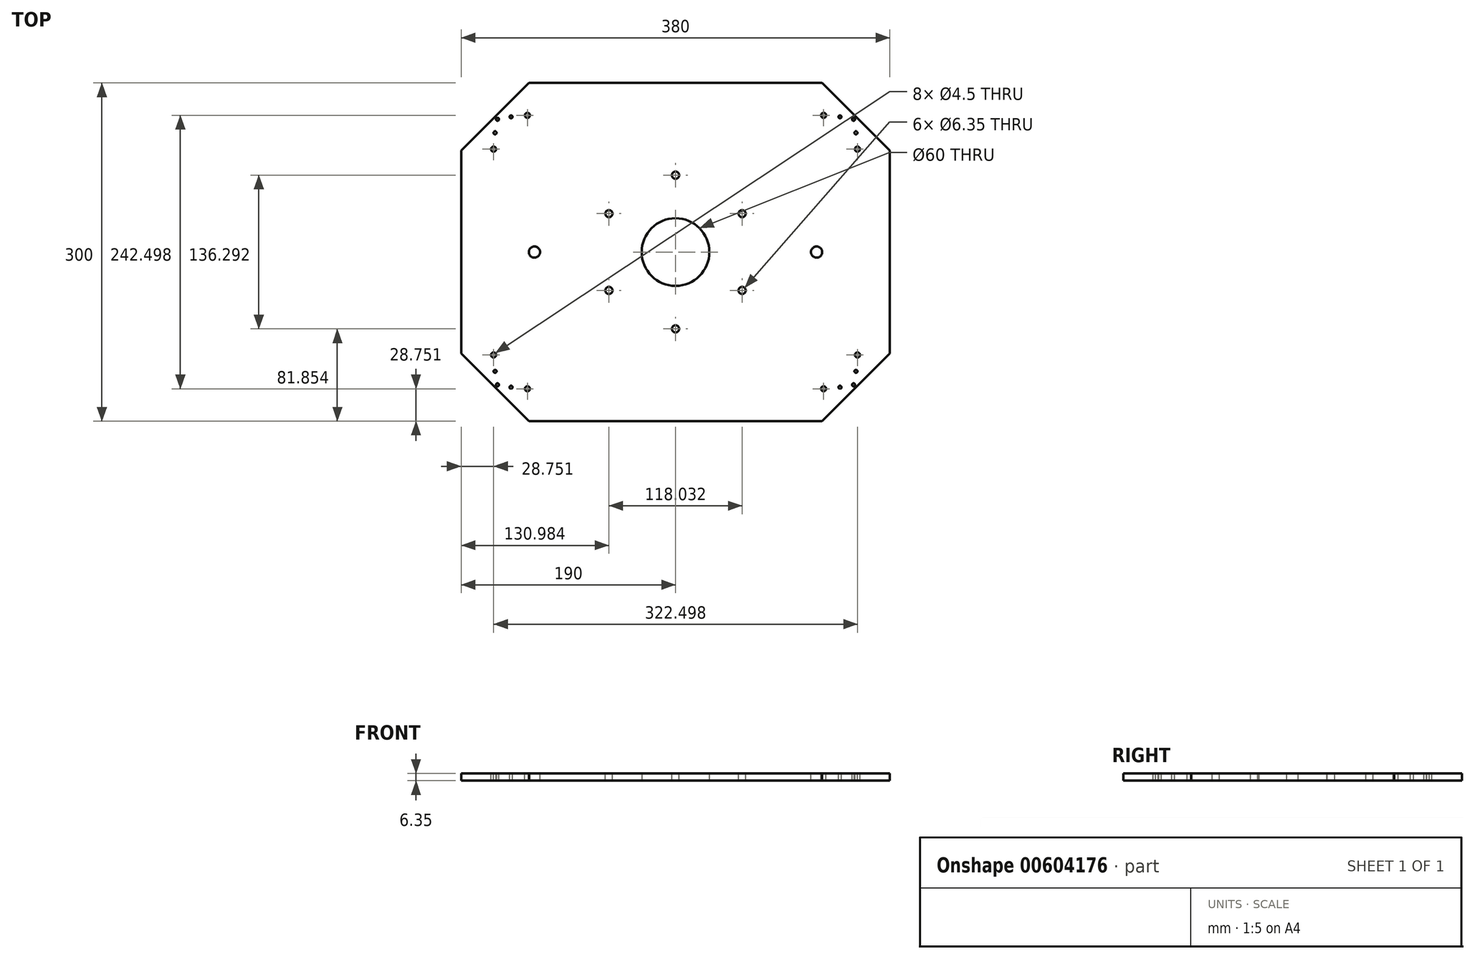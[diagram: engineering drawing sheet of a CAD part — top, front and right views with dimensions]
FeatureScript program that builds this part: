
annotation { "Feature Type Name" : "Feature", "Feature Type Description" : "" }
export const myFeature = defineFeature(function(context is Context, id is Id, definition is map)
    precondition{}
    {
        {
            var Q0;
            Q0=qCreatedBy(makeId("Top.planeOp"),FACE);
            var sketch = newSketch(context, id + "F0", { "sketchPlane" : qUnion([Q0])});
            skLineSegment(sketch, "E0", {"start": v(-130, 0) * mm, "end": v(-190, 60) * mm});
            skLineSegment(sketch, "E1", {"start": v(-190, 60) * mm, "end": v(-190, 240) * mm});
            skLineSegment(sketch, "E2", {"start": v(-190, 240) * mm, "end": v(-130, 300) * mm});
            skLineSegment(sketch, "E3", {"start": v(-130, 300) * mm, "end": v(130, 300) * mm});
            skLineSegment(sketch, "E4", {"start": v(130, 300) * mm, "end": v(190, 240) * mm});
            skLineSegment(sketch, "E5", {"start": v(190, 240) * mm, "end": v(190, 60) * mm});
            skLineSegment(sketch, "E6", {"start": v(190, 60) * mm, "end": v(130, 0) * mm});
            skLineSegment(sketch, "E7", {"start": v(130, 0) * mm, "end": v(-130, 0) * mm});
            skPoint(sketch, "E8.endSnap0", {"position": v(0, 300) * mm});
            skPoint(sketch, "E9.0.midPoint", {"position": v(0, 204.86) * mm});
            skPoint(sketch, "E10.0.midPoint", {"position": v(30.27, 157.38) * mm});
            skLineSegment(sketch, "E11", {"start": v(-190, 150) * mm, "end": v(190, 150) * mm, "construction": true});
            skLineSegment(sketch, "E12", {"start": v(0, 300) * mm, "end": v(0, 0) * mm, "construction": true});
            skCircle(sketch, "E13", {"center": v(0, 150) * mm, "radius": 30 * mm});
            skSolve(sketch);
        }
        {
            var Q0;
            Q0=qSketchRegion(id+"F0",true);
            extrude(context, id + "F1", {"entities" : qUnion([Q0]), "depth" : 6.35 * mm, "offsetDistance" : 25 * mm});
        }
        {
            var Q0;
            {var subQ0=sQuery(id+"F0.wireOp",EDGE,"E2");var subQ1=sQuery(id+"F0.wireOp",EDGE,"E1");var subQ2=sQuery(id+"F0.wireOp",EDGE,"E3");var subQ3=sQuery(id+"F0.wireOp",EDGE,"E0");var subQ4=sQuery(id+"F0.wireOp",EDGE,"E4");var subQ5=sQuery(id+"F0.wireOp",EDGE,"E5");var subQ6=sQuery(id+"F0.wireOp",EDGE,"E6");var subQ7=sQuery(id+"F0.wireOp",EDGE,"E7");Q0=makeQuery(id+"FAH0EIdtt6uSNSP_1.boolean.opBoolean","SPLIT",FACE,{"disambiguationData":[TD([makeQuery(id+"F1.opExtrude","SWEPT_FACE",FACE,{"disambiguationData":[OSD([subQ3])]})])],"derivedFrom":makeQuery(id+"F1.opExtrude","CAP_FACE",FACE,{"disambiguationData":[OSD([subQ3,subQ1,subQ0,subQ2,subQ4,subQ5,subQ6,subQ7,sQuery(id+"F0.wireOp",EDGE,"E10.0"),sQuery(id+"F0.wireOp",EDGE,"E10.1"),sQuery(id+"F0.wireOp",EDGE,"E10.2"),sQuery(id+"F0.wireOp",EDGE,"E10.3"),sQuery(id+"F0.wireOp",EDGE,"E10.4"),sQuery(id+"F0.wireOp",EDGE,"E10.5")])],"isStart":false})});}
            var sketch = newSketch(context, id + "F2", { "sketchPlane" : qUnion([Q0])});
            skLineSegment(sketch, "E14", {"start": v(-190, 150) * mm, "end": v(190, 150) * mm, "construction": true});
            skPoint(sketch, "E15", {"position": v(0, 150) * mm});
            skPoint(sketch, "E16", {"position": v(-125, 150) * mm});
            skPoint(sketch, "E17", {"position": v(125, 150) * mm});
            skSolve(sketch);
        }
        {
            var Q0;
            Q0=sQuery(id+"F2.wireOp",VERTEX,"E16");
            var Q1;
            Q1=sQuery(id+"F2.wireOp",VERTEX,"E17");
            var Q2;
            Q2=makeQuery(id+"F1.opExtrude","SWEPT_BODY",BODY,{"disambiguationData":[OSD([sQuery(id+"F0.wireOp",EDGE,"E0"),sQuery(id+"F0.wireOp",EDGE,"E1"),sQuery(id+"F0.wireOp",EDGE,"E2"),sQuery(id+"F0.wireOp",EDGE,"E3"),sQuery(id+"F0.wireOp",EDGE,"E4"),sQuery(id+"F0.wireOp",EDGE,"E5"),sQuery(id+"F0.wireOp",EDGE,"E6"),sQuery(id+"F0.wireOp",EDGE,"E7"),sQuery(id+"F0.wireOp",EDGE,"E10.0"),sQuery(id+"F0.wireOp",EDGE,"E10.1"),sQuery(id+"F0.wireOp",EDGE,"E10.2"),sQuery(id+"F0.wireOp",EDGE,"E10.3"),sQuery(id+"F0.wireOp",EDGE,"E10.4"),sQuery(id+"F0.wireOp",EDGE,"E10.5")])]});
            hole(context, id + "F3", {"style" : HoleStyle.SIMPLE, "endStyle" : HoleEndStyle.THROUGH, "holeDiameter" : 10 * mm, "majorDiameter" : 3.17 * mm, "isTappedThrough" : true, "tappedDepth" : 12 * mm, "tapClearance" : 3, "locations" : qUnion([Q0, Q1]), "scope" : qUnion([Q2])});
        }
        {
            var Q0;
            {var subQ0=sQuery(id+"F0.wireOp",EDGE,"E2");var subQ1=sQuery(id+"F0.wireOp",EDGE,"E1");var subQ2=sQuery(id+"F0.wireOp",EDGE,"E3");var subQ3=sQuery(id+"F0.wireOp",EDGE,"E0");var subQ4=sQuery(id+"F0.wireOp",EDGE,"E4");var subQ5=sQuery(id+"F0.wireOp",EDGE,"E5");var subQ6=sQuery(id+"F0.wireOp",EDGE,"E6");var subQ7=sQuery(id+"F0.wireOp",EDGE,"E7");Q0=makeQuery(id+"FAH0EIdtt6uSNSP_1.boolean.opBoolean","SPLIT",FACE,{"disambiguationData":[TD([makeQuery(id+"F1.opExtrude","SWEPT_FACE",FACE,{"disambiguationData":[OSD([subQ3])]})])],"derivedFrom":makeQuery(id+"F1.opExtrude","CAP_FACE",FACE,{"disambiguationData":[OSD([subQ3,subQ1,subQ0,subQ2,subQ4,subQ5,subQ6,subQ7,sQuery(id+"F0.wireOp",EDGE,"E10.0"),sQuery(id+"F0.wireOp",EDGE,"E10.1"),sQuery(id+"F0.wireOp",EDGE,"E10.2"),sQuery(id+"F0.wireOp",EDGE,"E10.3"),sQuery(id+"F0.wireOp",EDGE,"E10.4"),sQuery(id+"F0.wireOp",EDGE,"E10.5")])],"isStart":false})});}
            var sketch = newSketch(context, id + "F4", { "sketchPlane" : qUnion([Q0])});
            skLineSegment(sketch, "E18", {"start": v(0, 300) * mm, "end": v(0, 0) * mm, "construction": true});
            skLineSegment(sketch, "E19", {"start": v(-190, 150) * mm, "end": v(190, 150) * mm, "construction": true});
            skPoint(sketch, "E20", {"position": v(0, 150) * mm});
            skLineSegment(sketch, "E21", {"start": v(121.25, 261.25) * mm, "end": v(0, 261.25) * mm, "construction": true});
            skLineSegment(sketch, "E22", {"start": v(121.25, 261.25) * mm, "end": v(121.25, 150) * mm, "construction": true});
            skLineSegment(sketch, "E23", {"start": v(151.25, 231.25) * mm, "end": v(151.25, 150) * mm, "construction": true});
            skLineSegment(sketch, "E24", {"start": v(151.25, 231.25) * mm, "end": v(0, 231.25) * mm, "construction": true});
            skPoint(sketch, "E25", {"position": v(121.25, 231.25) * mm});
            skLineSegment(sketch, "E26", {"start": v(121.25, 231.25) * mm, "end": v(142.93, 252.93) * mm, "construction": true});
            skLineSegment(sketch, "E27", {"start": v(142.93, 252.93) * mm, "end": v(150, 245.86) * mm, "construction": true});
            skLineSegment(sketch, "E28", {"start": v(142.93, 252.93) * mm, "end": v(135.86, 260) * mm, "construction": true});
            skLineSegment(sketch, "E29", {"start": v(142.93, 252.93) * mm, "end": v(147.75, 257.75) * mm, "construction": true});
            skLineSegment(sketch, "E30.MirrorCS", {"start": v(-121.25, 261.25) * mm, "end": v(0, 261.25) * mm, "construction": true});
            skLineSegment(sketch, "E31.MirrorCS", {"start": v(-151.25, 231.25) * mm, "end": v(0, 231.25) * mm, "construction": true});
            skLineSegment(sketch, "E32.MirrorCS", {"start": v(-121.25, 261.25) * mm, "end": v(-121.25, 150) * mm, "construction": true});
            skLineSegment(sketch, "E33.MirrorCS", {"start": v(-151.25, 231.25) * mm, "end": v(-151.25, 150) * mm, "construction": true});
            skLineSegment(sketch, "E34.MirrorCS", {"start": v(-121.25, 231.25) * mm, "end": v(-142.93, 252.93) * mm, "construction": true});
            skLineSegment(sketch, "E35.MirrorCS", {"start": v(-142.93, 252.93) * mm, "end": v(-135.86, 260) * mm, "construction": true});
            skLineSegment(sketch, "E36.MirrorCS", {"start": v(-142.93, 252.93) * mm, "end": v(-150, 245.86) * mm, "construction": true});
            skLineSegment(sketch, "E37.MirrorCS", {"start": v(-142.93, 252.93) * mm, "end": v(-147.75, 257.75) * mm, "construction": true});
            skLineSegment(sketch, "E38.MirrorCS", {"start": v(-142.93, 47.07) * mm, "end": v(-147.75, 42.25) * mm, "construction": true});
            skLineSegment(sketch, "E39.MirrorCS", {"start": v(-142.93, 47.07) * mm, "end": v(-135.86, 40) * mm, "construction": true});
            skLineSegment(sketch, "E40.MirrorCS", {"start": v(-142.93, 47.07) * mm, "end": v(-150, 54.14) * mm, "construction": true});
            skLineSegment(sketch, "E41.MirrorCS", {"start": v(-121.25, 68.75) * mm, "end": v(-142.93, 47.07) * mm, "construction": true});
            skLineSegment(sketch, "E42.MirrorCS", {"start": v(-151.25, 68.75) * mm, "end": v(0, 68.75) * mm, "construction": true});
            skLineSegment(sketch, "E43.MirrorCS", {"start": v(-151.25, 68.75) * mm, "end": v(-151.25, 150) * mm, "construction": true});
            skLineSegment(sketch, "E44.MirrorCS", {"start": v(-121.25, 38.75) * mm, "end": v(0, 38.75) * mm, "construction": true});
            skLineSegment(sketch, "E45.MirrorCS", {"start": v(-121.25, 38.75) * mm, "end": v(-121.25, 150) * mm, "construction": true});
            skLineSegment(sketch, "E46.MirrorCS", {"start": v(151.25, 68.75) * mm, "end": v(0, 68.75) * mm, "construction": true});
            skLineSegment(sketch, "E47.MirrorCS", {"start": v(121.25, 38.75) * mm, "end": v(0, 38.75) * mm, "construction": true});
            skLineSegment(sketch, "E48.MirrorCS", {"start": v(121.25, 38.75) * mm, "end": v(121.25, 150) * mm, "construction": true});
            skLineSegment(sketch, "E49.MirrorCS", {"start": v(151.25, 68.75) * mm, "end": v(151.25, 150) * mm, "construction": true});
            skLineSegment(sketch, "E50.MirrorCS", {"start": v(121.25, 68.75) * mm, "end": v(142.93, 47.07) * mm, "construction": true});
            skLineSegment(sketch, "E51.MirrorCS", {"start": v(142.93, 47.07) * mm, "end": v(150, 54.14) * mm, "construction": true});
            skLineSegment(sketch, "E52.MirrorCS", {"start": v(142.93, 47.07) * mm, "end": v(135.86, 40) * mm, "construction": true});
            skLineSegment(sketch, "E53.MirrorCS", {"start": v(142.93, 47.07) * mm, "end": v(147.75, 42.25) * mm, "construction": true});
            skLineSegment(sketch, "E54", {"start": v(-160, 270) * mm, "end": v(-157.75, 267.75) * mm, "construction": true});
            skLineSegment(sketch, "E55", {"start": v(-160, 30) * mm, "end": v(-157.75, 32.25) * mm, "construction": true});
            skLineSegment(sketch, "E56", {"start": v(160, 270) * mm, "end": v(157.75, 267.75) * mm, "construction": true});
            skLineSegment(sketch, "E57", {"start": v(160, 30) * mm, "end": v(157.75, 32.25) * mm, "construction": true});
            skLineSegment(sketch, "E58", {"start": v(160, 30) * mm, "end": v(130, 0) * mm, "construction": true});
            skLineSegment(sketch, "E59", {"start": v(130, 0) * mm, "end": v(145, 15) * mm, "construction": true});
            skLineSegment(sketch, "E60", {"start": v(145, 15) * mm, "end": v(131.25, 28.75) * mm, "construction": true});
            skLineSegment(sketch, "E61", {"start": v(190, 60) * mm, "end": v(160, 30) * mm, "construction": true});
            skLineSegment(sketch, "E62", {"start": v(175, 45) * mm, "end": v(161.25, 58.75) * mm, "construction": true});
            skLineSegment(sketch, "E63.MirrorCS", {"start": v(-145, 15) * mm, "end": v(-131.25, 28.75) * mm, "construction": true});
            skLineSegment(sketch, "E64.MirrorCS", {"start": v(-175, 45) * mm, "end": v(-161.25, 58.75) * mm, "construction": true});
            skLineSegment(sketch, "E65.MirrorCS", {"start": v(-145, 285) * mm, "end": v(-131.25, 271.25) * mm, "construction": true});
            skLineSegment(sketch, "E66.MirrorCS", {"start": v(-175, 255) * mm, "end": v(-161.25, 241.25) * mm, "construction": true});
            skLineSegment(sketch, "E67.MirrorCS", {"start": v(145, 285) * mm, "end": v(131.25, 271.25) * mm, "construction": true});
            skLineSegment(sketch, "E68.MirrorCS", {"start": v(175, 255) * mm, "end": v(161.25, 241.25) * mm, "construction": true});
            skLineSegment(sketch, "E69", {"start": v(-150, 245.86) * mm, "end": v(-148.23, 244.1) * mm, "construction": true});
            skLineSegment(sketch, "E70", {"start": v(-135.86, 260) * mm, "end": v(-134.1, 258.23) * mm, "construction": true});
            skLineSegment(sketch, "E71.MirrorCS", {"start": v(-150, 54.14) * mm, "end": v(-148.23, 55.9) * mm, "construction": true});
            skLineSegment(sketch, "E72.MirrorCS", {"start": v(-135.86, 40) * mm, "end": v(-134.1, 41.77) * mm, "construction": true});
            skLineSegment(sketch, "E73.MirrorCS", {"start": v(150, 245.86) * mm, "end": v(148.23, 244.1) * mm, "construction": true});
            skLineSegment(sketch, "E74.MirrorCS", {"start": v(135.86, 260) * mm, "end": v(134.1, 258.23) * mm, "construction": true});
            skLineSegment(sketch, "E75.MirrorCS", {"start": v(150, 54.14) * mm, "end": v(148.23, 55.9) * mm, "construction": true});
            skLineSegment(sketch, "E76.MirrorCS", {"start": v(135.86, 40) * mm, "end": v(134.1, 41.77) * mm, "construction": true});
            skLineSegment(sketch, "E77", {"start": v(-135.86, 40) * mm, "end": v(-145.76, 30.1) * mm, "construction": true});
            skLineSegment(sketch, "E78", {"start": v(-150, 54.14) * mm, "end": v(-159.9, 44.24) * mm, "construction": true});
            skLineSegment(sketch, "E79.MirrorCS", {"start": v(150, 54.14) * mm, "end": v(159.9, 44.24) * mm, "construction": true});
            skLineSegment(sketch, "E80.MirrorCS", {"start": v(135.86, 40) * mm, "end": v(145.76, 30.1) * mm, "construction": true});
            skLineSegment(sketch, "E81.MirrorCS", {"start": v(-150, 245.86) * mm, "end": v(-159.9, 255.76) * mm, "construction": true});
            skLineSegment(sketch, "E82.MirrorCS", {"start": v(-135.86, 260) * mm, "end": v(-145.76, 269.9) * mm, "construction": true});
            skLineSegment(sketch, "E83.MirrorCS", {"start": v(150, 245.86) * mm, "end": v(159.9, 255.76) * mm, "construction": true});
            skLineSegment(sketch, "E84.MirrorCS", {"start": v(135.86, 260) * mm, "end": v(145.76, 269.9) * mm, "construction": true});
            skSolve(sketch);
        }
        {
            var Q0;
            Q0=makeQuery(id+"F4.imprint","IMPRINT",FACE,{"disambiguationData":[TD([[makeQuery(id+"F4.imprint","IMPRINT",EDGE,{"derivedFrom":makeQuery(id+"F1.opExtrude","CAP_EDGE",EDGE,{"disambiguationData":[OSD([sQuery(id+"F0.wireOp",EDGE,"E0")])],"isStart":false})}),-1.0]])]});
            var sketch = newSketch(context, id + "F5", { "sketchPlane" : qUnion([Q0])});
            skCircle(sketch, "E85.cCircle", {"center": v(0, 150) * mm, "radius": 59.02 * mm, "construction": true});
            skLineSegment(sketch, "E85.0", {"start": v(0, 218.15) * mm, "end": v(59.02, 184.07) * mm});
            skLineSegment(sketch, "E85.1", {"start": v(59.02, 184.07) * mm, "end": v(59.02, 115.93) * mm});
            skLineSegment(sketch, "E85.2", {"start": v(59.02, 115.93) * mm, "end": v(0, 81.85) * mm});
            skLineSegment(sketch, "E85.3", {"start": v(0, 81.85) * mm, "end": v(-59.02, 115.93) * mm});
            skLineSegment(sketch, "E85.4", {"start": v(-59.02, 115.93) * mm, "end": v(-59.02, 184.07) * mm});
            skLineSegment(sketch, "E85.5", {"start": v(-59.02, 184.07) * mm, "end": v(0, 218.15) * mm});
            skPoint(sketch, "E85.0.midPoint", {"position": v(29.5, 201.1) * mm});
            skSolve(sketch);
        }
        {
            var Q0;
            Q0=sQuery(id+"F5.wireOp",VERTEX,"E85.5.end");
            var Q1;
            Q1=sQuery(id+"F5.wireOp",VERTEX,"E85.0.end");
            var Q2;
            Q2=sQuery(id+"F5.wireOp",VERTEX,"E85.5.start");
            var Q3;
            Q3=sQuery(id+"F5.wireOp",VERTEX,"E85.4.start");
            var Q4;
            Q4=sQuery(id+"F5.wireOp",VERTEX,"E85.2.end");
            var Q5;
            Q5=sQuery(id+"F5.wireOp",VERTEX,"E85.1.end");
            var Q6;
            Q6=makeQuery(id+"F1.opExtrude","SWEPT_BODY",BODY,{"disambiguationData":[OSD([sQuery(id+"F0.wireOp",EDGE,"E0"),sQuery(id+"F0.wireOp",EDGE,"E1"),sQuery(id+"F0.wireOp",EDGE,"E2"),sQuery(id+"F0.wireOp",EDGE,"E3"),sQuery(id+"F0.wireOp",EDGE,"E4"),sQuery(id+"F0.wireOp",EDGE,"E5"),sQuery(id+"F0.wireOp",EDGE,"E6"),sQuery(id+"F0.wireOp",EDGE,"E7"),sQuery(id+"F0.wireOp",EDGE,"E13")])]});
            hole(context, id + "F6", {"style" : HoleStyle.SIMPLE, "endStyle" : HoleEndStyle.THROUGH, "holeDiameter" : 6.35 * mm, "majorDiameter" : 3 * mm, "isTappedThrough" : true, "tappedDepth" : 12 * mm, "tapClearance" : 3, "locations" : qUnion([Q0, Q1, Q2, Q3, Q4, Q5]), "scope" : qUnion([Q6])});
        }
        {
            var Q0;
            Q0=sQuery(id+"F4.wireOp",VERTEX,"E66.MirrorCS.end");
            var Q1;
            Q1=sQuery(id+"F4.wireOp",VERTEX,"E65.MirrorCS.end");
            var Q2;
            Q2=sQuery(id+"F4.wireOp",VERTEX,"E64.MirrorCS.end");
            var Q3;
            Q3=sQuery(id+"F4.wireOp",VERTEX,"E63.MirrorCS.end");
            var Q4;
            Q4=sQuery(id+"F4.wireOp",VERTEX,"E60.end");
            var Q5;
            Q5=sQuery(id+"F4.wireOp",VERTEX,"E62.end");
            var Q6;
            Q6=sQuery(id+"F4.wireOp",VERTEX,"E68.MirrorCS.end");
            var Q7;
            Q7=sQuery(id+"F4.wireOp",VERTEX,"E67.MirrorCS.end");
            var Q8;
            Q8=makeQuery(id+"F1.opExtrude","SWEPT_BODY",BODY,{"disambiguationData":[OSD([sQuery(id+"F0.wireOp",EDGE,"E0"),sQuery(id+"F0.wireOp",EDGE,"E1"),sQuery(id+"F0.wireOp",EDGE,"E2"),sQuery(id+"F0.wireOp",EDGE,"E3"),sQuery(id+"F0.wireOp",EDGE,"E4"),sQuery(id+"F0.wireOp",EDGE,"E5"),sQuery(id+"F0.wireOp",EDGE,"E6"),sQuery(id+"F0.wireOp",EDGE,"E7"),sQuery(id+"F0.wireOp",EDGE,"E13")])]});
            hole(context, id + "F7", {"style" : HoleStyle.SIMPLE, "endStyle" : HoleEndStyle.THROUGH, "holeDiameter" : 4.5 * mm, "majorDiameter" : 5 * mm, "isTappedThrough" : true, "tappedDepth" : 12 * mm, "tapClearance" : 3, "locations" : qUnion([Q0, Q1, Q2, Q3, Q4, Q5, Q6, Q7]), "scope" : qUnion([Q8])});
        }
        {
            var Q0;
            Q0=sQuery(id+"F4.wireOp",VERTEX,"E56.end");
            var Q1;
            Q1=sQuery(id+"F4.wireOp",VERTEX,"E57.end");
            var Q2;
            Q2=sQuery(id+"F4.wireOp",VERTEX,"E55.end");
            var Q3;
            Q3=sQuery(id+"F4.wireOp",VERTEX,"E54.end");
            var Q4;
            Q4=makeQuery(id+"F1.opExtrude","SWEPT_BODY",BODY,{"disambiguationData":[OSD([sQuery(id+"F0.wireOp",EDGE,"E0"),sQuery(id+"F0.wireOp",EDGE,"E1"),sQuery(id+"F0.wireOp",EDGE,"E2"),sQuery(id+"F0.wireOp",EDGE,"E3"),sQuery(id+"F0.wireOp",EDGE,"E4"),sQuery(id+"F0.wireOp",EDGE,"E5"),sQuery(id+"F0.wireOp",EDGE,"E6"),sQuery(id+"F0.wireOp",EDGE,"E7"),sQuery(id+"F0.wireOp",EDGE,"E13")])]});
            hole(context, id + "F8", {"style" : HoleStyle.SIMPLE, "endStyle" : HoleEndStyle.THROUGH, "standardTappedOrClearance" : lookupTablePath({ "standard" : "ANSI", "engagement" : "75%", "pitch" : "32 tpi", "size" : "#6", "type" : "Tapped" }), "standardBlindInLast" : lookupTablePath({ "standard" : "ANSI", "engagement" : "75%", "pitch" : "32 tpi", "size" : "#6", "type" : "Tapped" }), "holeDiameter" : 2.7 * mm, "majorDiameter" : 3.5 * mm, "showTappedDepth" : true, "isTappedThrough" : true, "tappedDepth" : 12 * mm, "tapClearance" : 3, "locations" : qUnion([Q0, Q1, Q2, Q3]), "scope" : qUnion([Q4])});
        }
        {
            var Q0;
            Q0=sQuery(id+"F4.wireOp",VERTEX,"E81.MirrorCS.end");
            var Q1;
            Q1=sQuery(id+"F4.wireOp",VERTEX,"E82.MirrorCS.end");
            var Q2;
            Q2=sQuery(id+"F4.wireOp",VERTEX,"E78.end");
            var Q3;
            Q3=sQuery(id+"F4.wireOp",VERTEX,"E77.end");
            var Q4;
            Q4=sQuery(id+"F4.wireOp",VERTEX,"E80.MirrorCS.end");
            var Q5;
            Q5=sQuery(id+"F4.wireOp",VERTEX,"E79.MirrorCS.end");
            var Q6;
            Q6=sQuery(id+"F4.wireOp",VERTEX,"E84.MirrorCS.end");
            var Q7;
            Q7=sQuery(id+"F4.wireOp",VERTEX,"E83.MirrorCS.end");
            var Q8;
            Q8=makeQuery(id+"F1.opExtrude","SWEPT_BODY",BODY,{"disambiguationData":[OSD([sQuery(id+"F0.wireOp",EDGE,"E0"),sQuery(id+"F0.wireOp",EDGE,"E1"),sQuery(id+"F0.wireOp",EDGE,"E2"),sQuery(id+"F0.wireOp",EDGE,"E3"),sQuery(id+"F0.wireOp",EDGE,"E4"),sQuery(id+"F0.wireOp",EDGE,"E5"),sQuery(id+"F0.wireOp",EDGE,"E6"),sQuery(id+"F0.wireOp",EDGE,"E7"),sQuery(id+"F0.wireOp",EDGE,"E13")])]});
            hole(context, id + "F9", {"style" : HoleStyle.SIMPLE, "endStyle" : HoleEndStyle.THROUGH, "standardTappedOrClearance" : lookupTablePath({ "standard" : "ANSI", "engagement" : "75%", "pitch" : "32 tpi", "size" : "#6", "type" : "Tapped" }), "standardBlindInLast" : lookupTablePath({ "standard" : "ANSI", "engagement" : "75%", "pitch" : "32 tpi", "size" : "#6", "type" : "Tapped" }), "holeDiameter" : 2.7 * mm, "majorDiameter" : 3.5 * mm, "showTappedDepth" : true, "isTappedThrough" : true, "tappedDepth" : 12 * mm, "tapClearance" : 3, "locations" : qUnion([Q0, Q1, Q2, Q3, Q4, Q5, Q6, Q7]), "scope" : qUnion([Q8])});
        }
    });
